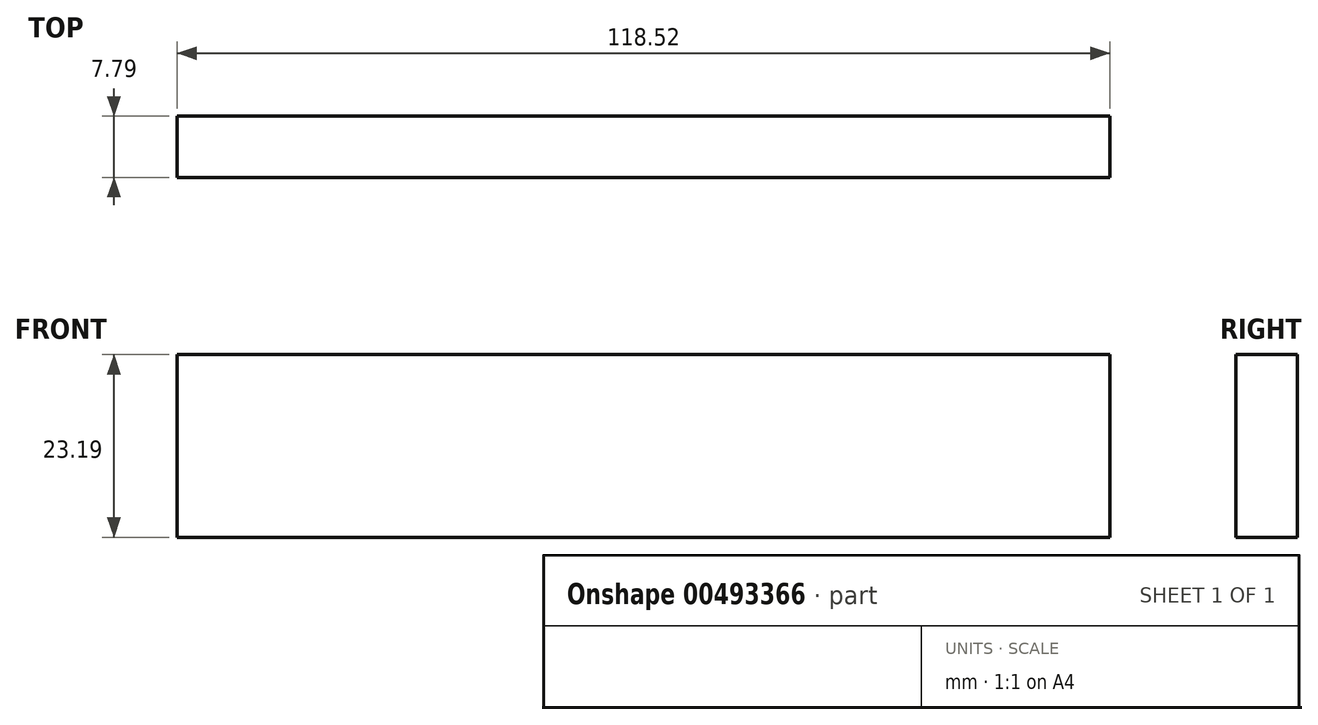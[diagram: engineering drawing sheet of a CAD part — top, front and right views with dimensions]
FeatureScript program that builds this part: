
annotation { "Feature Type Name" : "Feature", "Feature Type Description" : "" }
export const myFeature = defineFeature(function(context is Context, id is Id, definition is map)
    precondition{}
    {
        {
            var Q0;
            Q0=qCreatedBy(makeId("Front.planeOp"),FACE);
            var sketch = newSketch(context, id + "F0", { "sketchPlane" : qUnion([Q0])});
            skLineSegment(sketch, "E0.bottom", {"start": v(-63.69, -11.95) * mm, "end": v(54.83, -11.95) * mm});
            skLineSegment(sketch, "E0.top", {"start": v(-63.69, -35.14) * mm, "end": v(54.83, -35.14) * mm});
            skLineSegment(sketch, "E0.left", {"start": v(-63.69, -11.95) * mm, "end": v(-63.69, -35.14) * mm});
            skLineSegment(sketch, "E0.right", {"start": v(54.83, -11.95) * mm, "end": v(54.83, -35.14) * mm});
            skSolve(sketch);
        }
        {
            var Q0;
            Q0=makeQuery(id+"F0.imprint","IMPRINT",FACE,{"disambiguationData":[TD([[makeQuery(id+"F0.imprint","IMPRINT",EDGE,{"derivedFrom":sQuery(id+"F0.wireOp",EDGE,"E0.bottom")}),-1.0]])]});
            extrude(context, id + "F1", {"entities" : qUnion([Q0]), "depth" : 7.8 * mm});
        }
    });
